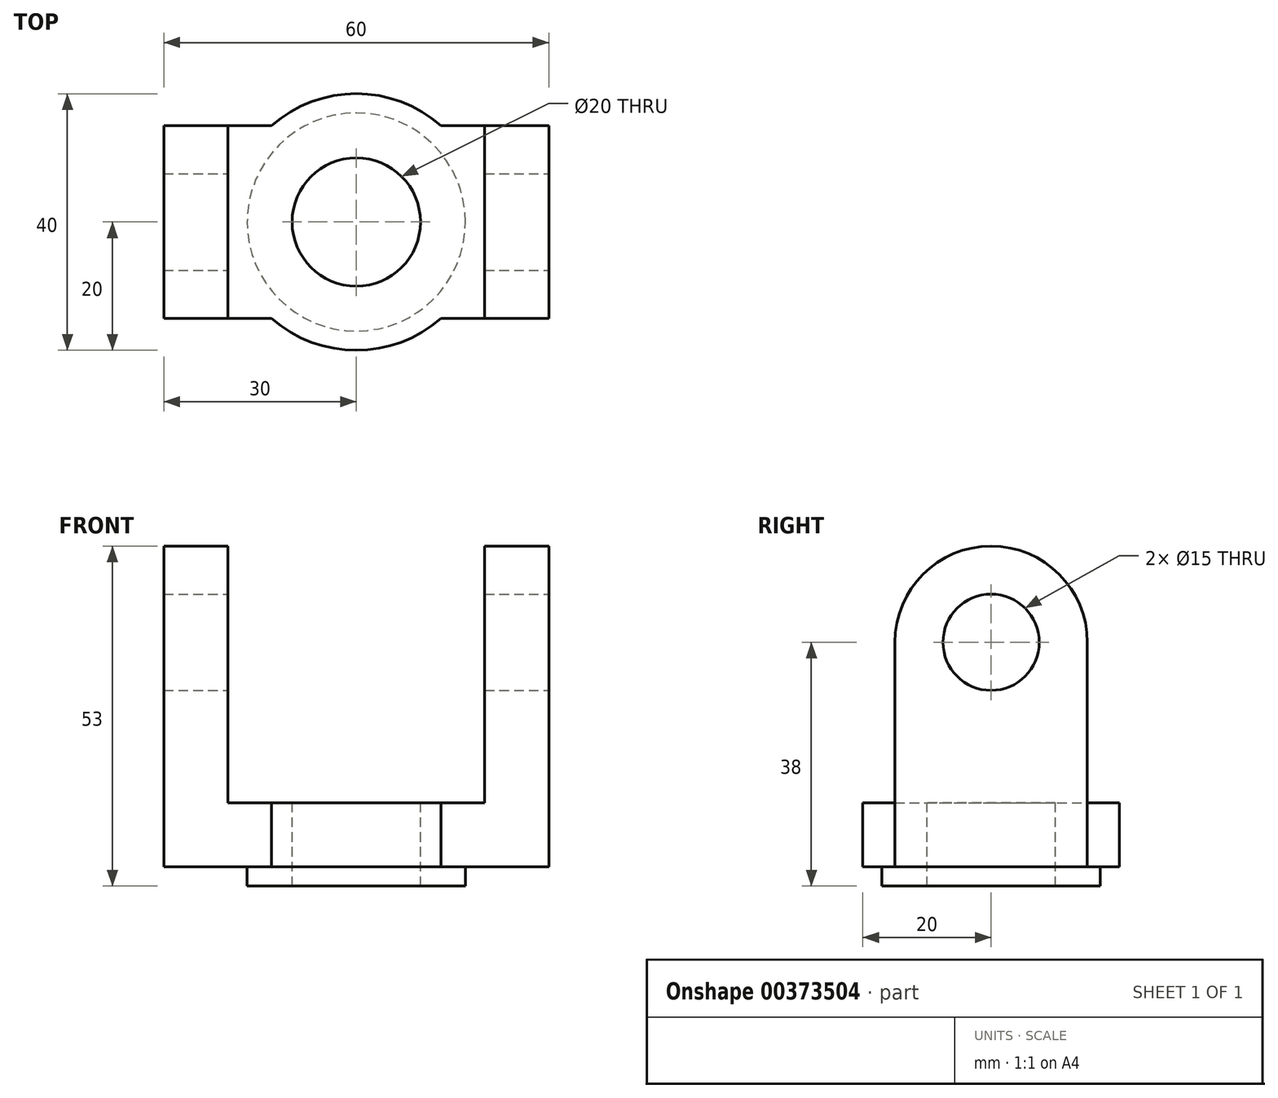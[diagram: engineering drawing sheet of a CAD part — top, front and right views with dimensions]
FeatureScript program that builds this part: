
annotation { "Feature Type Name" : "Feature", "Feature Type Description" : "" }
export const myFeature = defineFeature(function(context is Context, id is Id, definition is map)
    precondition{}
    {
        {
            var Q0;
            Q0=qCreatedBy(makeId("Front.planeOp"),FACE);
            var sketch = newSketch(context, id + "F0", { "sketchPlane" : qUnion([Q0])});
            skLineSegment(sketch, "E0", {"start": v(-30, 40) * mm, "end": v(-30, -10) * mm});
            skLineSegment(sketch, "E1", {"start": v(-30, -10) * mm, "end": v(30, -10) * mm});
            skLineSegment(sketch, "E2", {"start": v(30, -10) * mm, "end": v(30, 40) * mm});
            skLineSegment(sketch, "E3", {"start": v(30, 40) * mm, "end": v(20, 40) * mm});
            skLineSegment(sketch, "E4", {"start": v(20, 40) * mm, "end": v(20, 0) * mm});
            skLineSegment(sketch, "E5", {"start": v(20, 0) * mm, "end": v(-20, 0) * mm});
            skLineSegment(sketch, "E6", {"start": v(-20, 0) * mm, "end": v(-20, 40) * mm});
            skLineSegment(sketch, "E7", {"start": v(-20, 40) * mm, "end": v(-30, 40) * mm});
            skSolve(sketch);
        }
        {
            var Q0;
            Q0=makeQuery(id+"F0.imprint","IMPRINT",FACE,{"disambiguationData":[TD([[makeQuery(id+"F0.imprint","IMPRINT",EDGE,{"derivedFrom":sQuery(id+"F0.wireOp",EDGE,"E0")}),1.0]])]});
            extrude(context, id + "F1", {"entities" : qUnion([Q0]), "depth" : 30 * mm});
        }
        {
            var Q0;
            Q0=makeQuery(id+"F1.opExtrude","SWEPT_FACE",FACE,{"disambiguationData":[OSD([sQuery(id+"F0.wireOp",EDGE,"E2")])]});
            var sketch = newSketch(context, id + "F2", { "sketchPlane" : qUnion([Q0])});
            skCircle(sketch, "E8", {"center": v(-15, 25) * mm, "radius": 15 * mm});
            skPoint(sketch, "E8.centerSnap0", {"position": v(-15, 40) * mm});
            skCircle(sketch, "E9", {"center": v(-15, 25) * mm, "radius": 7.5 * mm});
            skLineSegment(sketch, "E10", {"start": v(-30, 20.07) * mm, "end": v(-30, 40) * mm});
            skLineSegment(sketch, "E11", {"start": v(-30, 40) * mm, "end": v(0, 40) * mm});
            skLineSegment(sketch, "E12", {"start": v(0, 40) * mm, "end": v(0, 17.76) * mm});
            skSolve(sketch);
        }
        {
            var Q0;
            {var subQ0=sQuery(id+"F2.wireOp",EDGE,"E11");var subQ1=sQuery(id+"F2.wireOp",EDGE,"E8");var subQ2=makeQuery(id+"F2.imprint","INTERSECT",VERTEX,{"derivedFrom":[subQ1,subQ0]});Q0=makeQuery(id+"F2.imprint","IMPRINT",FACE,{"disambiguationData":[TD([[makeQuery(id+"F2.imprint","IMPRINT",EDGE,{"disambiguationData":[TD([[subQ2,1.0]])],"derivedFrom":subQ1}),-1.0]])]});}
            var Q1;
            {var subQ0=sQuery(id+"F2.wireOp",EDGE,"E11");var subQ1=sQuery(id+"F2.wireOp",EDGE,"E8");var subQ2=makeQuery(id+"F2.imprint","INTERSECT",VERTEX,{"derivedFrom":[subQ1,subQ0]});Q1=makeQuery(id+"F2.imprint","IMPRINT",FACE,{"disambiguationData":[TD([[makeQuery(id+"F2.imprint","IMPRINT",EDGE,{"disambiguationData":[TD([[subQ2,-1.0]])],"derivedFrom":subQ1}),-1.0]])]});}
            var Q2;
            Q2=makeQuery(id+"F2.imprint","IMPRINT",FACE,{"disambiguationData":[TD([[makeQuery(id+"F2.imprint","IMPRINT",EDGE,{"derivedFrom":sQuery(id+"F2.wireOp",EDGE,"E9")}),1.0]])]});
            extrude(context, id + "F3", {"entities" : qUnion([Q0, Q1, Q2]), "operationType" : NewBodyOperationType.REMOVE, "endBound" : BoundingType.THROUGH_ALL, "oppositeDirection" : true, "depth" : 25 * mm});
        }
        {
            var Q0;
            Q0=makeQuery(id+"F1.opExtrude","SWEPT_FACE",FACE,{"disambiguationData":[OSD([sQuery(id+"F0.wireOp",EDGE,"E5")])]});
            var sketch = newSketch(context, id + "F4", { "sketchPlane" : qUnion([Q0])});
            skCircle(sketch, "E13", {"center": v(0, -15) * mm, "radius": 20 * mm});
            skSolve(sketch);
        }
        {
            var Q0;
            {var subQ0=sQuery(id+"F4.wireOp",EDGE,"E13");var subQ1=makeQuery(id+"F1.opExtrude","CAP_EDGE",EDGE,{"disambiguationData":[OSD([sQuery(id+"F0.wireOp",EDGE,"E5")])],"isStart":true});var subQ2=makeQuery(id+"F4.imprint","INTERSECT",VERTEX,{"disambiguationData":[OD(0.0)],"derivedFrom":[subQ1,subQ0]});Q0=makeQuery(id+"F4.imprint","IMPRINT",FACE,{"disambiguationData":[TD([[makeQuery(id+"F4.imprint","IMPRINT",EDGE,{"disambiguationData":[TD([[subQ2,1.0]])],"derivedFrom":subQ0}),1.0]])]});}
            var Q1;
            {var subQ0=sQuery(id+"F4.wireOp",EDGE,"E13");var subQ1=sQuery(id+"F0.wireOp",EDGE,"E5");var subQ2=makeQuery(id+"F1.opExtrude","CAP_EDGE",EDGE,{"disambiguationData":[OSD([subQ1])],"isStart":true});var subQ3=makeQuery(id+"F4.imprint","INTERSECT",VERTEX,{"disambiguationData":[OD(0.0)],"derivedFrom":[subQ2,subQ0]});Q1=makeQuery(id+"F4.imprint","IMPRINT",FACE,{"disambiguationData":[TD([[makeQuery(id+"F4.imprint","IMPRINT",EDGE,{"disambiguationData":[TD([[subQ3,-1.0]])],"derivedFrom":subQ0}),1.0]])]});}
            var Q2;
            {var subQ0=sQuery(id+"F4.wireOp",EDGE,"E13");var subQ1=makeQuery(id+"F1.opExtrude","CAP_EDGE",EDGE,{"disambiguationData":[OSD([sQuery(id+"F0.wireOp",EDGE,"E5")])],"isStart":false});var subQ2=makeQuery(id+"F4.imprint","INTERSECT",VERTEX,{"disambiguationData":[OD(0.0)],"derivedFrom":[subQ1,subQ0]});Q2=makeQuery(id+"F4.imprint","IMPRINT",FACE,{"disambiguationData":[TD([[makeQuery(id+"F4.imprint","IMPRINT",EDGE,{"disambiguationData":[TD([[subQ2,-1.0]])],"derivedFrom":subQ0}),1.0]])]});}
            var Q3;
            Q3=sQuery(id+"F4.wireOp",EDGE,"E13");
            extrude(context, id + "F5", {"entities" : qUnion([Q0, Q1, Q2]), "operationType" : NewBodyOperationType.ADD, "surfaceEntities" : qUnion([Q3]), "oppositeDirection" : true, "depth" : 10 * mm});
        }
        {
            var Q0;
            Q0=makeQuery(id+"F5.boolean.opBoolean","MERGE",FACE,{"derivedFrom":[makeQuery(id+"F1.opExtrude","SWEPT_FACE",FACE,{"disambiguationData":[OSD([sQuery(id+"F0.wireOp",EDGE,"E5")])]}),makeQuery(id+"F5.opExtrude","CAP_FACE",FACE,{"disambiguationData":[OSD([sQuery(id+"F4.wireOp",EDGE,"E13")])],"isStart":true})]});
            var sketch = newSketch(context, id + "F6", { "sketchPlane" : qUnion([Q0])});
            skCircle(sketch, "E14", {"center": v(0, -15) * mm, "radius": 10 * mm});
            skSolve(sketch);
        }
        {
            var Q0;
            Q0=makeQuery(id+"F6.imprint","IMPRINT",FACE,{"disambiguationData":[TD([[makeQuery(id+"F6.imprint","IMPRINT",EDGE,{"derivedFrom":sQuery(id+"F6.wireOp",EDGE,"E14")}),1.0]])]});
            extrude(context, id + "F7", {"entities" : qUnion([Q0]), "operationType" : NewBodyOperationType.REMOVE, "endBound" : BoundingType.THROUGH_ALL, "oppositeDirection" : true, "depth" : 25 * mm});
        }
        {
            var Q0;
            Q0=makeQuery(id+"F5.boolean.opBoolean","MERGE",FACE,{"derivedFrom":[makeQuery(id+"F1.opExtrude","SWEPT_FACE",FACE,{"disambiguationData":[OSD([sQuery(id+"F0.wireOp",EDGE,"E1")])]}),makeQuery(id+"F5.opExtrude","CAP_FACE",FACE,{"disambiguationData":[OSD([sQuery(id+"F4.wireOp",EDGE,"E13")])],"isStart":false})]});
            var sketch = newSketch(context, id + "F8", { "sketchPlane" : qUnion([Q0])});
            skCircle(sketch, "E15", {"center": v(0, 15) * mm, "radius": 17 * mm});
            skSolve(sketch);
        }
        {
            var Q0;
            Q0=makeQuery(id+"F8.imprint","IMPRINT",FACE,{"disambiguationData":[TD([[makeQuery(id+"F8.imprint","IMPRINT",EDGE,{"derivedFrom":sQuery(id+"F8.wireOp",EDGE,"E15")}),1.0]])]});
            var Q1;
            Q1=sQuery(id+"F8.wireOp",EDGE,"E15");
            extrude(context, id + "F9", {"entities" : qUnion([Q0]), "operationType" : NewBodyOperationType.ADD, "surfaceEntities" : qUnion([Q1]), "depth" : 3 * mm});
        }
    });
